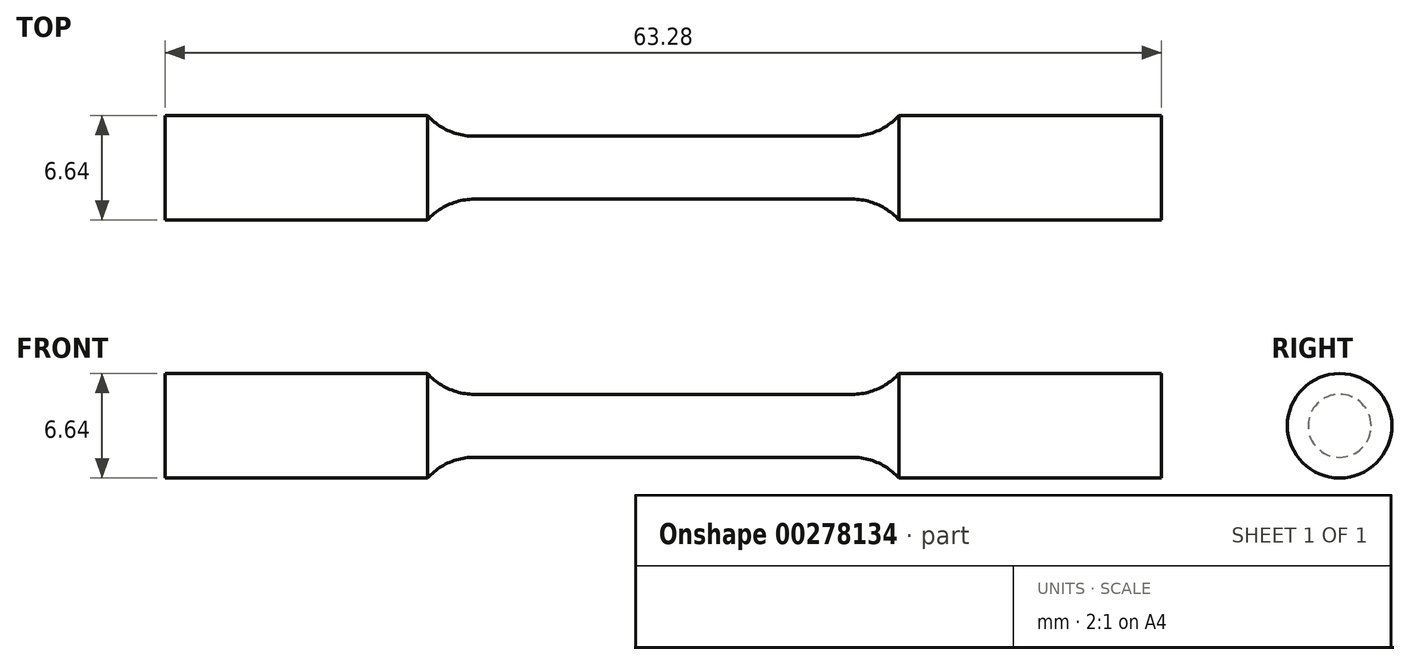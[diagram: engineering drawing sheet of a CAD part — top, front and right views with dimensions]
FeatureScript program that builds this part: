
annotation { "Feature Type Name" : "Feature", "Feature Type Description" : "" }
export const myFeature = defineFeature(function(context is Context, id is Id, definition is map)
    precondition{}
    {
        {
            var Q0;
            Q0=qCreatedBy(makeId("Front.planeOp"),FACE);
            var sketch = newSketch(context, id + "F0", { "sketchPlane" : qUnion([Q0])});
            skLineSegment(sketch, "E0", {"start": v(0, 2) * mm, "end": v(12, 2) * mm});
            skArc(sketch, "E1", {"start": v(12, 2) * mm, "mid": v(13.62, 2.34) * mm, "end": v(14.97, 3.32) * mm});
            skLineSegment(sketch, "E2", {"start": v(14.97, 3.32) * mm, "end": v(31.64, 3.32) * mm});
            skLineSegment(sketch, "E3", {"start": v(31.64, 3.32) * mm, "end": v(31.64, 0) * mm});
            skLineSegment(sketch, "E4.MirrorCS", {"start": v(0, 2) * mm, "end": v(-12, 2) * mm});
            skLineSegment(sketch, "E5.MirrorCS", {"start": v(-31.64, 3.32) * mm, "end": v(-31.64, 0) * mm});
            skLineSegment(sketch, "E6.MirrorCS", {"start": v(-14.97, 3.32) * mm, "end": v(-31.64, 3.32) * mm});
            skArc(sketch, "E7.MirrorCS", {"start": v(-12, 2) * mm, "mid": v(-13.62, 2.34) * mm, "end": v(-14.97, 3.32) * mm});
            skLineSegment(sketch, "E8", {"start": v(-31.64, 0) * mm, "end": v(31.64, 0) * mm});
            skSolve(sketch);
        }
        {
            var Q0;
            Q0 = qSketchRegion(id + "F0", true);
            var Q1;
            Q1=sQuery(id+"F0.wireOp",EDGE,"E8");
            revolve(context, id + "F1", {"entities" : qUnion([Q0]), "axis" : qUnion([Q1]), "revolveType" : RevolveType.FULL});
        }
    });
